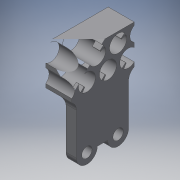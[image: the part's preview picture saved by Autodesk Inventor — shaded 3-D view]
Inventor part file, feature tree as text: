
AUTODESK INVENTOR PART (.ipt)
format: ipt  version: 2016 (Build 200138000, 138)  size: 284,672 bytes
history: native  units: in
note: dims shown in document units (in); Inventor stores cm internally (conversion verified against a paired STEP export)
features: reference x25, extrude x3, sketch x3, fillet x1
ambient origin geometry x8: Origin, YZ Plane, XZ Plane, XY Plane, X Axis, Y Axis, Z Axis, Center Point
bodies: Body1 (feature_tree)
feature tree (32):
  extrude  "Extrusion2"  Depth=0.1299in
  sketch  "Sketch2"  dims[d2=0.1299in d3=0.1299in]
  extrude  "Extrusion4"  Depth=0.1299in
  extrude  "Extrusion5"  Depth=0.0787in
  fillet  "Fillet1"  Radius=0.1592in
  sketch  "Sketch1"  dims[d0=0.1299in d1=0.1299in]
  reference  "Reference1"
  reference  "Reference2"
  reference  "Reference3"
  reference  "Reference4"
  reference  "Reference5"
  reference  "Reference6"
  reference  "Reference7"
  reference  "Reference8"
  reference  "Reference9"
  reference  "Reference10"
  reference  "Reference11"
  reference  "Reference12"
  reference  "Reference13"
  reference  "Reference14"
  reference  "Reference15"
  reference  "Reference16"
  reference  "Reference17"
  reference  "Reference18"
  reference  "Reference19"
  reference  "Reference20"
  reference  "Reference21"
  sketch  "Sketch3"  dims[d4=0.1299in d5=0.1299in d6=0.1592in d7=0.154in d8=0.1592in d9=0.154in d10=0.1299in d11=0.154in d14=0.1299in d15=0.154in d16=0.1969in d17=0.0in d18=0.2886in d19=0.2886in d20=0.2886in d21=0.2886in d23=0.2886in d24=0.2886in d25=15.0deg d26=15.0deg d27=15.0deg d28=15.0deg d29=15.0deg d30=0.0591in d31=0.0591in d32=0.0591in d33=0.0591in d34=0.0591in d35=0.0591in d38=0.0787in d39=0.0in d40=0.0591in d41=0.0in d42=0.0787in]
  reference  "Reference22"
  reference  "Reference23"
  reference  "Reference24"
  reference  "Reference25"
